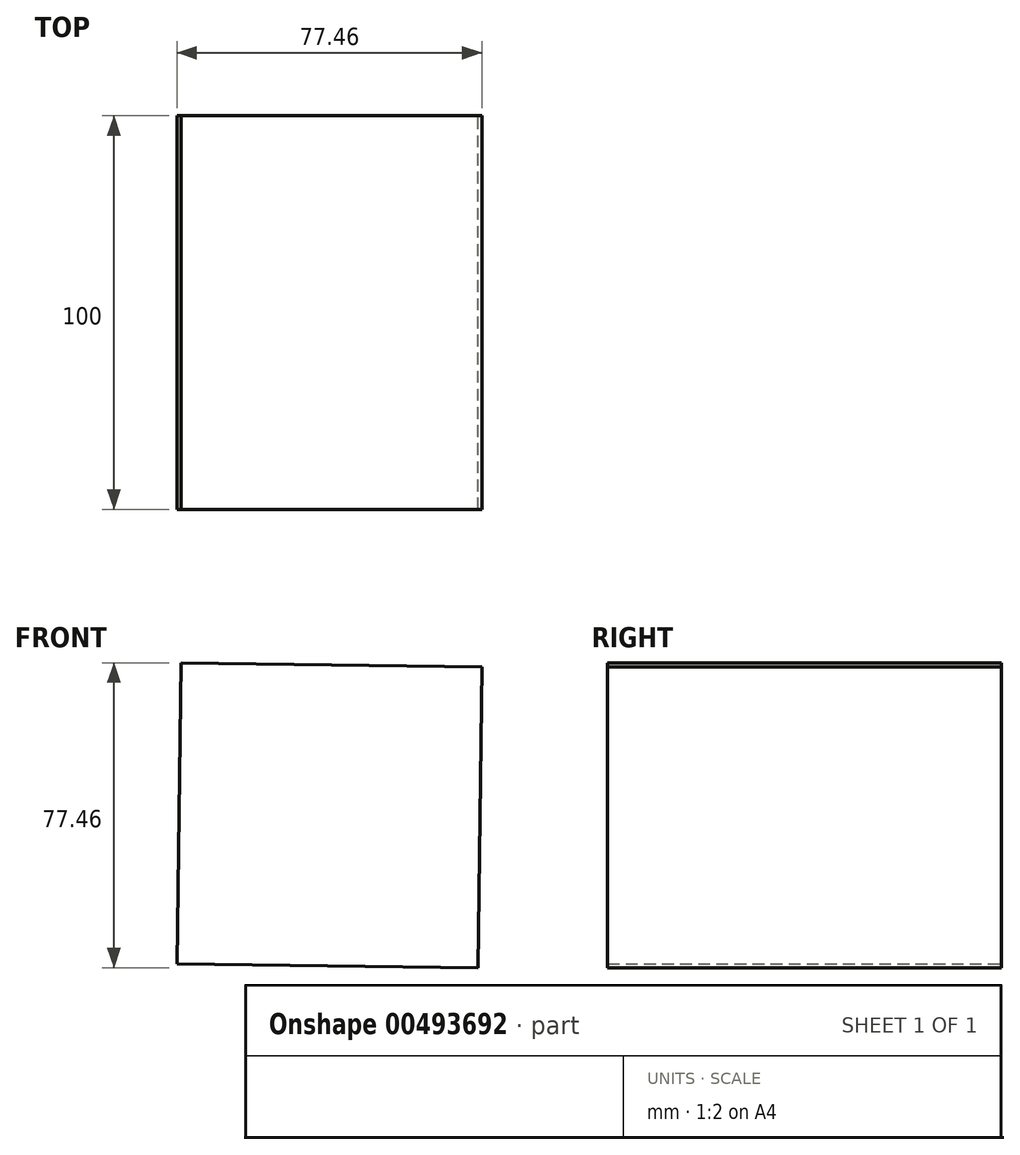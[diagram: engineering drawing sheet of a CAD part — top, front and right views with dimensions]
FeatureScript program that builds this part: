
annotation { "Feature Type Name" : "Feature", "Feature Type Description" : "" }
export const myFeature = defineFeature(function(context is Context, id is Id, definition is map)
    precondition{}
    {
        {
            var Q0;
            Q0=qCreatedBy(makeId("Front.planeOp"),FACE);
            var sketch = newSketch(context, id + "F0", { "sketchPlane" : qUnion([Q0])});
            skCircle(sketch, "E0.cCircle", {"center": v(0, 0) * mm, "radius": 54.07 * mm, "construction": true});
            skLineSegment(sketch, "E0.0", {"start": v(-37.73, 38.73) * mm, "end": v(38.73, 37.73) * mm});
            skLineSegment(sketch, "E0.1", {"start": v(38.73, 37.73) * mm, "end": v(37.73, -38.73) * mm});
            skLineSegment(sketch, "E0.2", {"start": v(37.73, -38.73) * mm, "end": v(-38.73, -37.73) * mm});
            skLineSegment(sketch, "E0.3", {"start": v(-38.73, -37.73) * mm, "end": v(-37.73, 38.73) * mm});
            skSolve(sketch);
        }
        {
            var Q0;
            Q0=makeQuery(id+"F0.imprint","IMPRINT",FACE,{"disambiguationData":[TD([[makeQuery(id+"F0.imprint","IMPRINT",EDGE,{"derivedFrom":sQuery(id+"F0.wireOp",EDGE,"E0.0")}),-1.0]])]});
            extrude(context, id + "F1", {"entities" : qUnion([Q0]), "depth" : 100 * mm});
        }
    });
